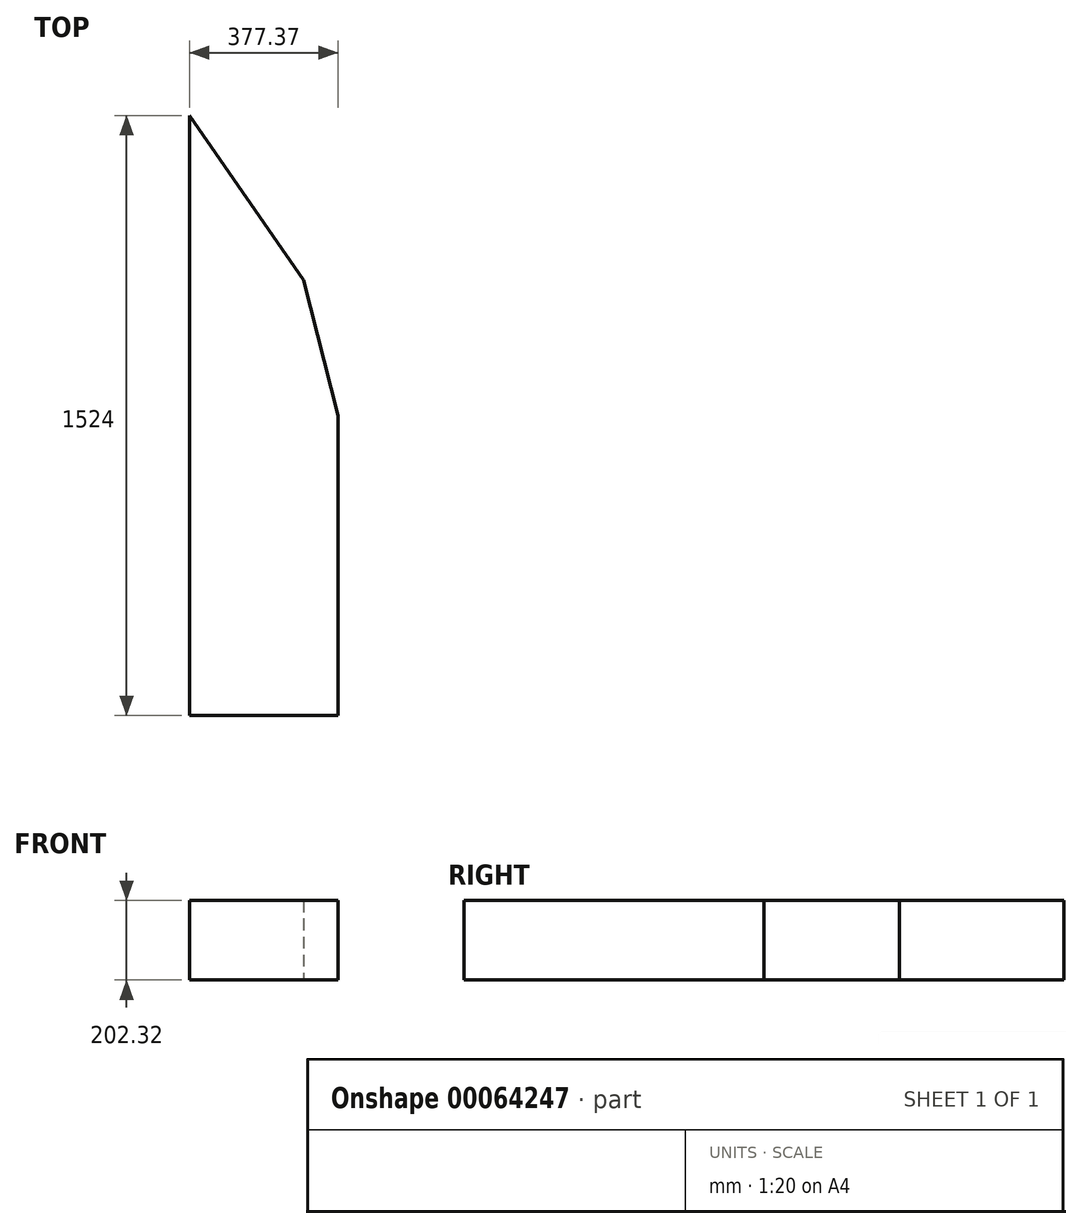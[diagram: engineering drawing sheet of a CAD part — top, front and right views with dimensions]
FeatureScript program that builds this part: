
annotation { "Feature Type Name" : "Feature", "Feature Type Description" : "" }
export const myFeature = defineFeature(function(context is Context, id is Id, definition is map)
    precondition{}
    {
        {
            var Q0;
            Q0=qCreatedBy(makeId("Top.planeOp"),FACE);
            var sketch = newSketch(context, id + "F0", { "sketchPlane" : qUnion([Q0])});
            skLineSegment(sketch, "E0", {"start": v(0, 0) * mm, "end": v(87.85, -344.58) * mm});
            skLineSegment(sketch, "E1", {"start": v(87.85, -344.58) * mm, "end": v(87.85, -1106.58) * mm});
            skLineSegment(sketch, "E2", {"start": v(87.85, -1106.58) * mm, "end": v(-289.52, -1106.58) * mm});
            skLineSegment(sketch, "E3", {"start": v(-289.52, -1106.58) * mm, "end": v(-289.52, 417.42) * mm});
            skLineSegment(sketch, "E4", {"start": v(-289.52, 417.42) * mm, "end": v(0, 0) * mm});
            skSolve(sketch);
        }
        {
            var Q0;
            Q0=makeQuery(id+"F0.imprint","IMPRINT",FACE,{"disambiguationData":[TD([[makeQuery(id+"F0.imprint","IMPRINT",EDGE,{"derivedFrom":sQuery(id+"F0.wireOp",EDGE,"E0")}),-1.0]])]});
            extrude(context, id + "F1", {"entities" : qUnion([Q0]), "depth" : 202.32 * mm});
        }
    });
